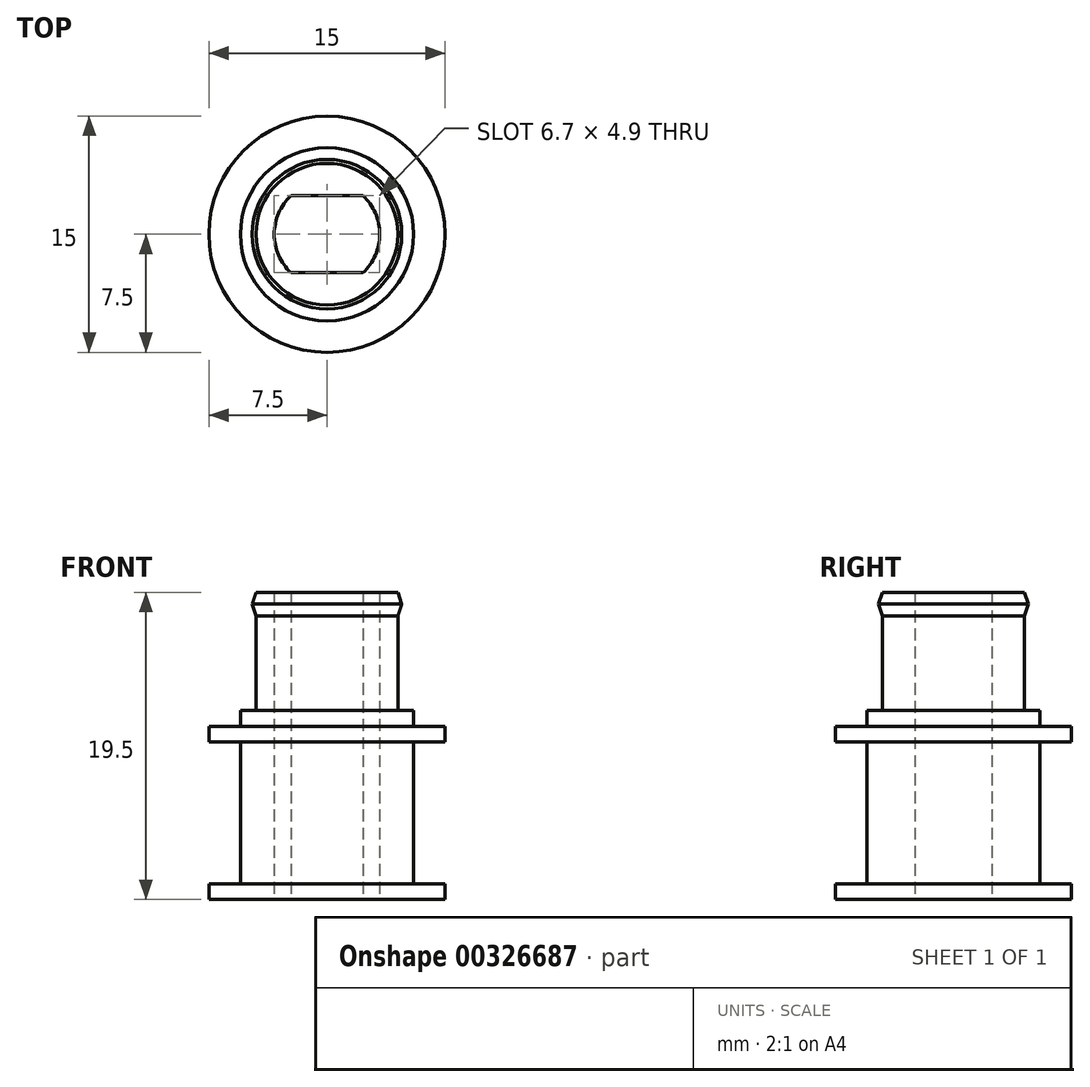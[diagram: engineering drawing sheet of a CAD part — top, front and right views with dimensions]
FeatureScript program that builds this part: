
annotation { "Feature Type Name" : "Feature", "Feature Type Description" : "" }
export const myFeature = defineFeature(function(context is Context, id is Id, definition is map)
    precondition{}
    {
        {
            var Q0;
            Q0=qCreatedBy(makeId("Top.planeOp"),FACE);
            var sketch = newSketch(context, id + "F0", { "sketchPlane" : qUnion([Q0])});
            skCircle(sketch, "E0", {"center": v(0, 0) * mm, "radius": 5.5 * mm});
            skCircle(sketch, "E1", {"center": v(0, 0) * mm, "radius": 4.5 * mm});
            skArc(sketch, "E2", {"start": v(-2.28, 2.45) * mm, "mid": v(-3.35, 0) * mm, "end": v(-2.28, -2.45) * mm});
            skLineSegment(sketch, "E3.bottom", {"start": v(2.28, -2.45) * mm, "end": v(-2.28, -2.45) * mm});
            skLineSegment(sketch, "E3.top", {"start": v(2.28, 2.45) * mm, "end": v(-2.28, 2.45) * mm});
            skArc(sketch, "E4.trimOffspring", {"start": v(2.28, -2.45) * mm, "mid": v(3.35, 0) * mm, "end": v(2.28, 2.45) * mm});
            skPoint(sketch, "E5.orphan", {"position": v(3.35, 2.45) * mm});
            skPoint(sketch, "E6.orphan", {"position": v(3.35, -2.45) * mm});
            skPoint(sketch, "E7.orphan", {"position": v(-3.35, -2.45) * mm});
            skPoint(sketch, "E8.orphan", {"position": v(-3.35, 2.45) * mm});
            skCircle(sketch, "E9", {"center": v(0, 0) * mm, "radius": 7.5 * mm});
            skSolve(sketch);
        }
        {
            var Q0;
            Q0=makeQuery(id+"F0.imprint","IMPRINT",FACE,{"disambiguationData":[TD([[makeQuery(id+"F0.imprint","IMPRINT",EDGE,{"derivedFrom":sQuery(id+"F0.wireOp",EDGE,"E9")}),1.0]])]});
            var Q1;
            Q1=makeQuery(id+"F0.imprint","IMPRINT",FACE,{"disambiguationData":[TD([[makeQuery(id+"F0.imprint","IMPRINT",EDGE,{"derivedFrom":sQuery(id+"F0.wireOp",EDGE,"E0")}),-1.0]])]});
            var Q2;
            Q2=makeQuery(id+"F0.imprint","IMPRINT",FACE,{"disambiguationData":[TD([[makeQuery(id+"F0.imprint","IMPRINT",EDGE,{"derivedFrom":sQuery(id+"F0.wireOp",EDGE,"E0")}),1.0]])]});
            var Q3;
            Q3=makeQuery(id+"F0.imprint","IMPRINT",FACE,{"disambiguationData":[TD([[makeQuery(id+"F0.imprint","IMPRINT",EDGE,{"derivedFrom":sQuery(id+"F0.wireOp",EDGE,"E1")}),1.0]])]});
            extrude(context, id + "F1", {"entities" : qUnion([Q0, Q1, Q2, Q3]), "depth" : 1 * mm});
        }
        {
            var Q0;
            Q0=makeQuery(id+"F1.opExtrude","SWEPT_BODY",BODY,{"disambiguationData":[OSD([sQuery(id+"F0.wireOp",EDGE,"E9"),sQuery(id+"F0.wireOp",EDGE,"EIqunKHo-nNsy-NuN7-MCyh-zDvAt2EbuDEc"),sQuery(id+"F0.wireOp",EDGE,"wDOxUPXS-ZM6U-Q8Jq-wcH9-EKwYlBhU692d"),sQuery(id+"F0.wireOp",EDGE,"eb7e76fe-5503-4f90-a268-9aebf731f32b0.MirrorCS"),sQuery(id+"F0.wireOp",EDGE,"KeFLWRGC-2lTl-id6V-Nq3M-w2rfNKTJ84NE"),sQuery(id+"F0.wireOp",EDGE,"b117cb93-11e5-48b8-9008-3f88b5f9d245.trimOffspring"),sQuery(id+"F0.wireOp",EDGE,"ce234f76-c4db-484e-b82a-35bcf09fa61d.1.0"),sQuery(id+"F0.wireOp",EDGE,"ce234f76-c4db-484e-b82a-35bcf09fa61d.1.1"),sQuery(id+"F0.wireOp",EDGE,"ce234f76-c4db-484e-b82a-35bcf09fa61d.1.2"),sQuery(id+"F0.wireOp",EDGE,"ce234f76-c4db-484e-b82a-35bcf09fa61d.1.3"),sQuery(id+"F0.wireOp",EDGE,"ce234f76-c4db-484e-b82a-35bcf09fa61d.1.4"),sQuery(id+"F0.wireOp",EDGE,"ce234f76-c4db-484e-b82a-35bcf09fa61d.2.0"),sQuery(id+"F0.wireOp",EDGE,"ce234f76-c4db-484e-b82a-35bcf09fa61d.2.1"),sQuery(id+"F0.wireOp",EDGE,"ce234f76-c4db-484e-b82a-35bcf09fa61d.2.2"),sQuery(id+"F0.wireOp",EDGE,"ce234f76-c4db-484e-b82a-35bcf09fa61d.2.3"),sQuery(id+"F0.wireOp",EDGE,"ce234f76-c4db-484e-b82a-35bcf09fa61d.2.4"),sQuery(id+"F0.wireOp",EDGE,"ce234f76-c4db-484e-b82a-35bcf09fa61d.3.0"),sQuery(id+"F0.wireOp",EDGE,"ce234f76-c4db-484e-b82a-35bcf09fa61d.3.1"),sQuery(id+"F0.wireOp",EDGE,"ce234f76-c4db-484e-b82a-35bcf09fa61d.3.2"),sQuery(id+"F0.wireOp",EDGE,"ce234f76-c4db-484e-b82a-35bcf09fa61d.3.3"),sQuery(id+"F0.wireOp",EDGE,"ce234f76-c4db-484e-b82a-35bcf09fa61d.3.4"),sQuery(id+"F0.wireOp",EDGE,"ce234f76-c4db-484e-b82a-35bcf09fa61d.4.0"),sQuery(id+"F0.wireOp",EDGE,"ce234f76-c4db-484e-b82a-35bcf09fa61d.4.1"),sQuery(id+"F0.wireOp",EDGE,"ce234f76-c4db-484e-b82a-35bcf09fa61d.4.2"),sQuery(id+"F0.wireOp",EDGE,"ce234f76-c4db-484e-b82a-35bcf09fa61d.4.3"),sQuery(id+"F0.wireOp",EDGE,"ce234f76-c4db-484e-b82a-35bcf09fa61d.4.4"),sQuery(id+"F0.wireOp",EDGE,"ce234f76-c4db-484e-b82a-35bcf09fa61d.5.0"),sQuery(id+"F0.wireOp",EDGE,"ce234f76-c4db-484e-b82a-35bcf09fa61d.5.1"),sQuery(id+"F0.wireOp",EDGE,"ce234f76-c4db-484e-b82a-35bcf09fa61d.5.2"),sQuery(id+"F0.wireOp",EDGE,"ce234f76-c4db-484e-b82a-35bcf09fa61d.5.3"),sQuery(id+"F0.wireOp",EDGE,"ce234f76-c4db-484e-b82a-35bcf09fa61d.5.4"),sQuery(id+"F0.wireOp",EDGE,"ce234f76-c4db-484e-b82a-35bcf09fa61d.6.0"),sQuery(id+"F0.wireOp",EDGE,"ce234f76-c4db-484e-b82a-35bcf09fa61d.6.1"),sQuery(id+"F0.wireOp",EDGE,"ce234f76-c4db-484e-b82a-35bcf09fa61d.6.2"),sQuery(id+"F0.wireOp",EDGE,"ce234f76-c4db-484e-b82a-35bcf09fa61d.6.3"),sQuery(id+"F0.wireOp",EDGE,"ce234f76-c4db-484e-b82a-35bcf09fa61d.6.4"),sQuery(id+"F0.wireOp",EDGE,"ce234f76-c4db-484e-b82a-35bcf09fa61d.7.0"),sQuery(id+"F0.wireOp",EDGE,"ce234f76-c4db-484e-b82a-35bcf09fa61d.7.1"),sQuery(id+"F0.wireOp",EDGE,"ce234f76-c4db-484e-b82a-35bcf09fa61d.7.2"),sQuery(id+"F0.wireOp",EDGE,"ce234f76-c4db-484e-b82a-35bcf09fa61d.7.3"),sQuery(id+"F0.wireOp",EDGE,"ce234f76-c4db-484e-b82a-35bcf09fa61d.7.4"),sQuery(id+"F0.wireOp",EDGE,"ce234f76-c4db-484e-b82a-35bcf09fa61d.8.0"),sQuery(id+"F0.wireOp",EDGE,"ce234f76-c4db-484e-b82a-35bcf09fa61d.8.1"),sQuery(id+"F0.wireOp",EDGE,"ce234f76-c4db-484e-b82a-35bcf09fa61d.8.2"),sQuery(id+"F0.wireOp",EDGE,"ce234f76-c4db-484e-b82a-35bcf09fa61d.8.3"),sQuery(id+"F0.wireOp",EDGE,"ce234f76-c4db-484e-b82a-35bcf09fa61d.8.4"),sQuery(id+"F0.wireOp",EDGE,"ce234f76-c4db-484e-b82a-35bcf09fa61d.9.0"),sQuery(id+"F0.wireOp",EDGE,"ce234f76-c4db-484e-b82a-35bcf09fa61d.9.1"),sQuery(id+"F0.wireOp",EDGE,"ce234f76-c4db-484e-b82a-35bcf09fa61d.9.2"),sQuery(id+"F0.wireOp",EDGE,"ce234f76-c4db-484e-b82a-35bcf09fa61d.9.3"),sQuery(id+"F0.wireOp",EDGE,"ce234f76-c4db-484e-b82a-35bcf09fa61d.9.4"),sQuery(id+"F0.wireOp",EDGE,"ce234f76-c4db-484e-b82a-35bcf09fa61d.10.0"),sQuery(id+"F0.wireOp",EDGE,"ce234f76-c4db-484e-b82a-35bcf09fa61d.10.1"),sQuery(id+"F0.wireOp",EDGE,"ce234f76-c4db-484e-b82a-35bcf09fa61d.10.2"),sQuery(id+"F0.wireOp",EDGE,"ce234f76-c4db-484e-b82a-35bcf09fa61d.10.3"),sQuery(id+"F0.wireOp",EDGE,"ce234f76-c4db-484e-b82a-35bcf09fa61d.10.4"),sQuery(id+"F0.wireOp",EDGE,"ce234f76-c4db-484e-b82a-35bcf09fa61d.11.0"),sQuery(id+"F0.wireOp",EDGE,"ce234f76-c4db-484e-b82a-35bcf09fa61d.11.1"),sQuery(id+"F0.wireOp",EDGE,"ce234f76-c4db-484e-b82a-35bcf09fa61d.11.2"),sQuery(id+"F0.wireOp",EDGE,"ce234f76-c4db-484e-b82a-35bcf09fa61d.11.3"),sQuery(id+"F0.wireOp",EDGE,"ce234f76-c4db-484e-b82a-35bcf09fa61d.11.4"),sQuery(id+"F0.wireOp",EDGE,"ce234f76-c4db-484e-b82a-35bcf09fa61d.12.0"),sQuery(id+"F0.wireOp",EDGE,"ce234f76-c4db-484e-b82a-35bcf09fa61d.12.1"),sQuery(id+"F0.wireOp",EDGE,"ce234f76-c4db-484e-b82a-35bcf09fa61d.12.2"),sQuery(id+"F0.wireOp",EDGE,"ce234f76-c4db-484e-b82a-35bcf09fa61d.12.3"),sQuery(id+"F0.wireOp",EDGE,"ce234f76-c4db-484e-b82a-35bcf09fa61d.12.4"),sQuery(id+"F0.wireOp",EDGE,"ce234f76-c4db-484e-b82a-35bcf09fa61d.13.0"),sQuery(id+"F0.wireOp",EDGE,"ce234f76-c4db-484e-b82a-35bcf09fa61d.13.1"),sQuery(id+"F0.wireOp",EDGE,"ce234f76-c4db-484e-b82a-35bcf09fa61d.13.2"),sQuery(id+"F0.wireOp",EDGE,"ce234f76-c4db-484e-b82a-35bcf09fa61d.13.3"),sQuery(id+"F0.wireOp",EDGE,"ce234f76-c4db-484e-b82a-35bcf09fa61d.13.4"),sQuery(id+"F0.wireOp",EDGE,"ce234f76-c4db-484e-b82a-35bcf09fa61d.14.0"),sQuery(id+"F0.wireOp",EDGE,"ce234f76-c4db-484e-b82a-35bcf09fa61d.14.1"),sQuery(id+"F0.wireOp",EDGE,"ce234f76-c4db-484e-b82a-35bcf09fa61d.14.2"),sQuery(id+"F0.wireOp",EDGE,"ce234f76-c4db-484e-b82a-35bcf09fa61d.14.3"),sQuery(id+"F0.wireOp",EDGE,"ce234f76-c4db-484e-b82a-35bcf09fa61d.14.4"),sQuery(id+"F0.wireOp",EDGE,"ce234f76-c4db-484e-b82a-35bcf09fa61d.15.0"),sQuery(id+"F0.wireOp",EDGE,"ce234f76-c4db-484e-b82a-35bcf09fa61d.15.1"),sQuery(id+"F0.wireOp",EDGE,"ce234f76-c4db-484e-b82a-35bcf09fa61d.15.2"),sQuery(id+"F0.wireOp",EDGE,"ce234f76-c4db-484e-b82a-35bcf09fa61d.15.3"),sQuery(id+"F0.wireOp",EDGE,"ce234f76-c4db-484e-b82a-35bcf09fa61d.15.4"),sQuery(id+"F0.wireOp",EDGE,"ce234f76-c4db-484e-b82a-35bcf09fa61d.16.0"),sQuery(id+"F0.wireOp",EDGE,"ce234f76-c4db-484e-b82a-35bcf09fa61d.16.1"),sQuery(id+"F0.wireOp",EDGE,"ce234f76-c4db-484e-b82a-35bcf09fa61d.16.2"),sQuery(id+"F0.wireOp",EDGE,"ce234f76-c4db-484e-b82a-35bcf09fa61d.16.3"),sQuery(id+"F0.wireOp",EDGE,"ce234f76-c4db-484e-b82a-35bcf09fa61d.16.4"),sQuery(id+"F0.wireOp",EDGE,"ce234f76-c4db-484e-b82a-35bcf09fa61d.17.0"),sQuery(id+"F0.wireOp",EDGE,"ce234f76-c4db-484e-b82a-35bcf09fa61d.17.1"),sQuery(id+"F0.wireOp",EDGE,"ce234f76-c4db-484e-b82a-35bcf09fa61d.17.2"),sQuery(id+"F0.wireOp",EDGE,"ce234f76-c4db-484e-b82a-35bcf09fa61d.17.3"),sQuery(id+"F0.wireOp",EDGE,"ce234f76-c4db-484e-b82a-35bcf09fa61d.17.4"),sQuery(id+"F0.wireOp",EDGE,"ce234f76-c4db-484e-b82a-35bcf09fa61d.18.0"),sQuery(id+"F0.wireOp",EDGE,"ce234f76-c4db-484e-b82a-35bcf09fa61d.18.1"),sQuery(id+"F0.wireOp",EDGE,"ce234f76-c4db-484e-b82a-35bcf09fa61d.18.2"),sQuery(id+"F0.wireOp",EDGE,"ce234f76-c4db-484e-b82a-35bcf09fa61d.18.3"),sQuery(id+"F0.wireOp",EDGE,"ce234f76-c4db-484e-b82a-35bcf09fa61d.18.4"),sQuery(id+"F0.wireOp",EDGE,"ce234f76-c4db-484e-b82a-35bcf09fa61d.19.0"),sQuery(id+"F0.wireOp",EDGE,"ce234f76-c4db-484e-b82a-35bcf09fa61d.19.1"),sQuery(id+"F0.wireOp",EDGE,"ce234f76-c4db-484e-b82a-35bcf09fa61d.19.2"),sQuery(id+"F0.wireOp",EDGE,"ce234f76-c4db-484e-b82a-35bcf09fa61d.19.3"),sQuery(id+"F0.wireOp",EDGE,"ce234f76-c4db-484e-b82a-35bcf09fa61d.19.4"),sQuery(id+"F0.wireOp",EDGE,"ce234f76-c4db-484e-b82a-35bcf09fa61d.20.0"),sQuery(id+"F0.wireOp",EDGE,"ce234f76-c4db-484e-b82a-35bcf09fa61d.20.1"),sQuery(id+"F0.wireOp",EDGE,"ce234f76-c4db-484e-b82a-35bcf09fa61d.20.2"),sQuery(id+"F0.wireOp",EDGE,"ce234f76-c4db-484e-b82a-35bcf09fa61d.20.3"),sQuery(id+"F0.wireOp",EDGE,"ce234f76-c4db-484e-b82a-35bcf09fa61d.20.4"),sQuery(id+"F0.wireOp",EDGE,"ce234f76-c4db-484e-b82a-35bcf09fa61d.21.0"),sQuery(id+"F0.wireOp",EDGE,"ce234f76-c4db-484e-b82a-35bcf09fa61d.21.1"),sQuery(id+"F0.wireOp",EDGE,"ce234f76-c4db-484e-b82a-35bcf09fa61d.21.2"),sQuery(id+"F0.wireOp",EDGE,"ce234f76-c4db-484e-b82a-35bcf09fa61d.21.3"),sQuery(id+"F0.wireOp",EDGE,"ce234f76-c4db-484e-b82a-35bcf09fa61d.21.4"),sQuery(id+"F0.wireOp",EDGE,"ce234f76-c4db-484e-b82a-35bcf09fa61d.22.0"),sQuery(id+"F0.wireOp",EDGE,"ce234f76-c4db-484e-b82a-35bcf09fa61d.22.1"),sQuery(id+"F0.wireOp",EDGE,"ce234f76-c4db-484e-b82a-35bcf09fa61d.22.2"),sQuery(id+"F0.wireOp",EDGE,"ce234f76-c4db-484e-b82a-35bcf09fa61d.22.3"),sQuery(id+"F0.wireOp",EDGE,"ce234f76-c4db-484e-b82a-35bcf09fa61d.22.4"),sQuery(id+"F0.wireOp",EDGE,"ce234f76-c4db-484e-b82a-35bcf09fa61d.23.0"),sQuery(id+"F0.wireOp",EDGE,"ce234f76-c4db-484e-b82a-35bcf09fa61d.23.1"),sQuery(id+"F0.wireOp",EDGE,"ce234f76-c4db-484e-b82a-35bcf09fa61d.23.2"),sQuery(id+"F0.wireOp",EDGE,"ce234f76-c4db-484e-b82a-35bcf09fa61d.23.3"),sQuery(id+"F0.wireOp",EDGE,"ce234f76-c4db-484e-b82a-35bcf09fa61d.23.4"),sQuery(id+"F0.wireOp",EDGE,"ce234f76-c4db-484e-b82a-35bcf09fa61d.24.0"),sQuery(id+"F0.wireOp",EDGE,"ce234f76-c4db-484e-b82a-35bcf09fa61d.24.1"),sQuery(id+"F0.wireOp",EDGE,"ce234f76-c4db-484e-b82a-35bcf09fa61d.24.2"),sQuery(id+"F0.wireOp",EDGE,"ce234f76-c4db-484e-b82a-35bcf09fa61d.24.3"),sQuery(id+"F0.wireOp",EDGE,"ce234f76-c4db-484e-b82a-35bcf09fa61d.24.4"),sQuery(id+"F0.wireOp",EDGE,"ce234f76-c4db-484e-b82a-35bcf09fa61d.25.0"),sQuery(id+"F0.wireOp",EDGE,"ce234f76-c4db-484e-b82a-35bcf09fa61d.25.1"),sQuery(id+"F0.wireOp",EDGE,"ce234f76-c4db-484e-b82a-35bcf09fa61d.25.2"),sQuery(id+"F0.wireOp",EDGE,"ce234f76-c4db-484e-b82a-35bcf09fa61d.25.3"),sQuery(id+"F0.wireOp",EDGE,"ce234f76-c4db-484e-b82a-35bcf09fa61d.25.4"),sQuery(id+"F0.wireOp",EDGE,"ce234f76-c4db-484e-b82a-35bcf09fa61d.26.0"),sQuery(id+"F0.wireOp",EDGE,"ce234f76-c4db-484e-b82a-35bcf09fa61d.26.1"),sQuery(id+"F0.wireOp",EDGE,"ce234f76-c4db-484e-b82a-35bcf09fa61d.26.2"),sQuery(id+"F0.wireOp",EDGE,"ce234f76-c4db-484e-b82a-35bcf09fa61d.26.3"),sQuery(id+"F0.wireOp",EDGE,"ce234f76-c4db-484e-b82a-35bcf09fa61d.26.4"),sQuery(id+"F0.wireOp",EDGE,"ce234f76-c4db-484e-b82a-35bcf09fa61d.27.0"),sQuery(id+"F0.wireOp",EDGE,"ce234f76-c4db-484e-b82a-35bcf09fa61d.27.1"),sQuery(id+"F0.wireOp",EDGE,"ce234f76-c4db-484e-b82a-35bcf09fa61d.27.2"),sQuery(id+"F0.wireOp",EDGE,"ce234f76-c4db-484e-b82a-35bcf09fa61d.27.3"),sQuery(id+"F0.wireOp",EDGE,"ce234f76-c4db-484e-b82a-35bcf09fa61d.27.4"),sQuery(id+"F0.wireOp",EDGE,"ce234f76-c4db-484e-b82a-35bcf09fa61d.28.0"),sQuery(id+"F0.wireOp",EDGE,"ce234f76-c4db-484e-b82a-35bcf09fa61d.28.1"),sQuery(id+"F0.wireOp",EDGE,"ce234f76-c4db-484e-b82a-35bcf09fa61d.28.2"),sQuery(id+"F0.wireOp",EDGE,"ce234f76-c4db-484e-b82a-35bcf09fa61d.28.3"),sQuery(id+"F0.wireOp",EDGE,"ce234f76-c4db-484e-b82a-35bcf09fa61d.28.4"),sQuery(id+"F0.wireOp",EDGE,"ce234f76-c4db-484e-b82a-35bcf09fa61d.29.0"),sQuery(id+"F0.wireOp",EDGE,"ce234f76-c4db-484e-b82a-35bcf09fa61d.29.1"),sQuery(id+"F0.wireOp",EDGE,"ce234f76-c4db-484e-b82a-35bcf09fa61d.29.2"),sQuery(id+"F0.wireOp",EDGE,"ce234f76-c4db-484e-b82a-35bcf09fa61d.29.3"),sQuery(id+"F0.wireOp",EDGE,"ce234f76-c4db-484e-b82a-35bcf09fa61d.29.4")])]});
            transform(context, id + "F2", {"entities" : qUnion([Q0]), "transformType" : TransformType.TRANSLATION_3D, "dx" : 0 * mm, "dy" : 0 * mm, "dz" : 10 * mm, "makeCopy" : true});
        }
        {
            var Q0;
            Q0=makeQuery(id+"F0.imprint","IMPRINT",FACE,{"disambiguationData":[TD([[makeQuery(id+"F0.imprint","IMPRINT",EDGE,{"derivedFrom":sQuery(id+"F0.wireOp",EDGE,"E0")}),1.0]])]});
            var Q1;
            Q1=makeQuery(id+"F0.imprint","IMPRINT",FACE,{"disambiguationData":[TD([[makeQuery(id+"F0.imprint","IMPRINT",EDGE,{"derivedFrom":sQuery(id+"F0.wireOp",EDGE,"E1")}),1.0]])]});
            extrude(context, id + "F3", {"entities" : qUnion([Q0, Q1]), "depth" : 12 * mm});
        }
        {
            var Q0;
            Q0=makeQuery(id+"F0.imprint","IMPRINT",FACE,{"disambiguationData":[TD([[makeQuery(id+"F0.imprint","IMPRINT",EDGE,{"derivedFrom":sQuery(id+"F0.wireOp",EDGE,"E1")}),1.0]])]});
            extrude(context, id + "F4", {"entities" : qUnion([Q0]), "operationType" : NewBodyOperationType.ADD, "depth" : 19.5 * mm});
        }
        {
            var Q0;
            Q0=qCreatedBy(makeId("Front.planeOp"),FACE);
            var sketch = newSketch(context, id + "F5", { "sketchPlane" : qUnion([Q0])});
            skLineSegment(sketch, "E10", {"start": v(0, 0) * mm, "end": v(0, 17.5) * mm, "construction": true});
            skLineSegment(sketch, "E11", {"start": v(-4.5, 6) * mm, "end": v(-4.5, 12.5) * mm});
            skLineSegment(sketch, "E12", {"start": v(4.5, 19.5) * mm, "end": v(4.5, 6) * mm});
            skLineSegment(sketch, "E13.bottom", {"start": v(4.5, 19.5) * mm, "end": v(4.75, 19.5) * mm, "construction": true});
            skLineSegment(sketch, "E13.top", {"start": v(4.5, 18) * mm, "end": v(4.75, 18) * mm, "construction": true});
            skLineSegment(sketch, "E13.left", {"start": v(4.5, 19.5) * mm, "end": v(4.5, 18) * mm, "construction": true});
            skLineSegment(sketch, "E13.right", {"start": v(4.75, 19.5) * mm, "end": v(4.75, 18) * mm, "construction": true});
            skPoint(sketch, "E14", {"position": v(4.75, 18.75) * mm});
            skLineSegment(sketch, "E15", {"start": v(4.5, 19.5) * mm, "end": v(4.75, 18.75) * mm});
            skLineSegment(sketch, "E16", {"start": v(4.75, 18.75) * mm, "end": v(4.5, 18) * mm});
            skLineSegment(sketch, "E17", {"start": v(4.5, 18) * mm, "end": v(4.5, 19.5) * mm});
            skSolve(sketch);
        }
        {
            var Q0;
            Q0=makeQuery(id+"F5.imprint","IMPRINT",FACE,{"disambiguationData":[TD([[makeQuery(id+"F5.imprint","IMPRINT",EDGE,{"derivedFrom":sQuery(id+"F5.wireOp",EDGE,"E15")}),-1.0]])]});
            var Q1;
            Q1=sQuery(id+"F5.wireOp",EDGE,"E10");
            revolve(context, id + "F6", {"operationType" : NewBodyOperationType.ADD, "entities" : qUnion([Q0]), "axis" : qUnion([Q1]), "revolveType" : RevolveType.FULL});
        }
        {
            var Q0;
            Q0=makeQuery(id+"F4.opExtrude","CAP_FACE",FACE,{"disambiguationData":[OSD([sQuery(id+"F0.wireOp",EDGE,"E1"),sQuery(id+"F0.wireOp",EDGE,"E2"),sQuery(id+"F0.wireOp",EDGE,"E3.bottom"),sQuery(id+"F0.wireOp",EDGE,"E3.top"),sQuery(id+"F0.wireOp",EDGE,"E4.trimOffspring")])],"isStart":false});
            cPlane(context, id + "F7", {"entities" : qUnion([Q0]), "cplaneType" : CPlaneType.OFFSET, "offset" : 0 * mm, "width" : 150 * mm, "height" : 150 * mm});
        }
        {
            var Q0;
            Q0=qCreatedBy(id+"F7.planeOp",FACE);
            var sketch = newSketch(context, id + "F8", { "sketchPlane" : qUnion([Q0])});
            skArc(sketch, "E18", {"start": v(-2.38, 2.7) * mm, "mid": v(-3.6, 0) * mm, "end": v(-2.38, -2.7) * mm});
            skLineSegment(sketch, "E19.bottom", {"start": v(-2.38, 2.7) * mm, "end": v(2.38, 2.7) * mm});
            skLineSegment(sketch, "E19.top", {"start": v(-2.38, -2.7) * mm, "end": v(2.38, -2.7) * mm});
            skPoint(sketch, "E20.orphan", {"position": v(4.18, 2.7) * mm});
            skPoint(sketch, "E21.orphan", {"position": v(3.52, -2.7) * mm});
            skArc(sketch, "E22.trimOffspring", {"start": v(2.38, -2.7) * mm, "mid": v(3.6, 0) * mm, "end": v(2.38, 2.7) * mm});
            skPoint(sketch, "E23.orphan", {"position": v(-4.18, -2.7) * mm});
            skPoint(sketch, "E24.orphan", {"position": v(-3.52, 2.7) * mm});
            skSolve(sketch);
        }
    });
